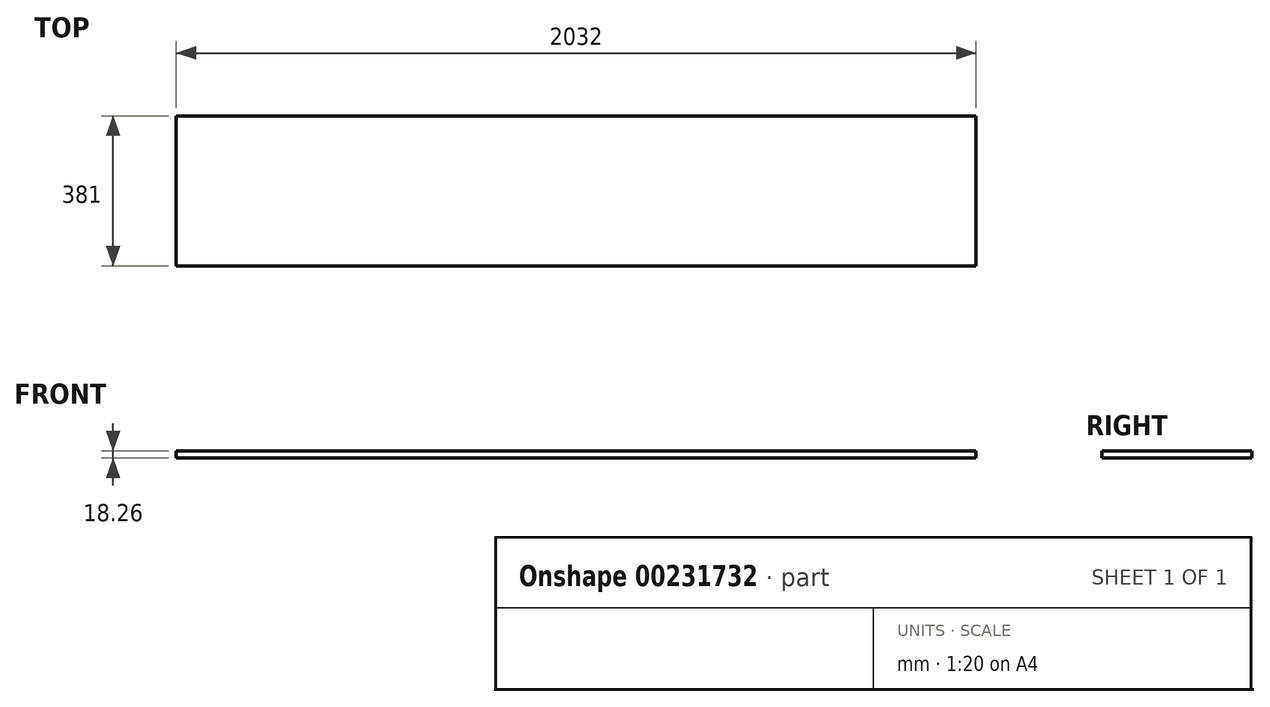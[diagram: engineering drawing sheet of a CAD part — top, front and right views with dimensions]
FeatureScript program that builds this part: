
annotation { "Feature Type Name" : "Feature", "Feature Type Description" : "" }
export const myFeature = defineFeature(function(context is Context, id is Id, definition is map)
    precondition{}
    {
        {
            var Q0;
            Q0=qCreatedBy(makeId("Top.planeOp"),FACE);
            var sketch = newSketch(context, id + "F0", { "sketchPlane" : qUnion([Q0])});
            skLineSegment(sketch, "E0.bottom", {"start": v(0, 0) * mm, "end": v(2032, 0) * mm});
            skLineSegment(sketch, "E0.top", {"start": v(0, 381) * mm, "end": v(2032, 381) * mm});
            skLineSegment(sketch, "E0.left", {"start": v(0, 0) * mm, "end": v(0, 381) * mm});
            skLineSegment(sketch, "E0.right", {"start": v(2032, 0) * mm, "end": v(2032, 381) * mm});
            skSolve(sketch);
        }
        {
            var Q0;
            Q0=makeQuery(id+"F0.imprint","IMPRINT",FACE,{"disambiguationData":[TD([[makeQuery(id+"F0.imprint","IMPRINT",EDGE,{"derivedFrom":sQuery(id+"F0.wireOp",EDGE,"E0.bottom")}),1.0]])]});
            extrude(context, id + "F1", {"entities" : qUnion([Q0]), "depth" : 18.26 * mm});
        }
    });
